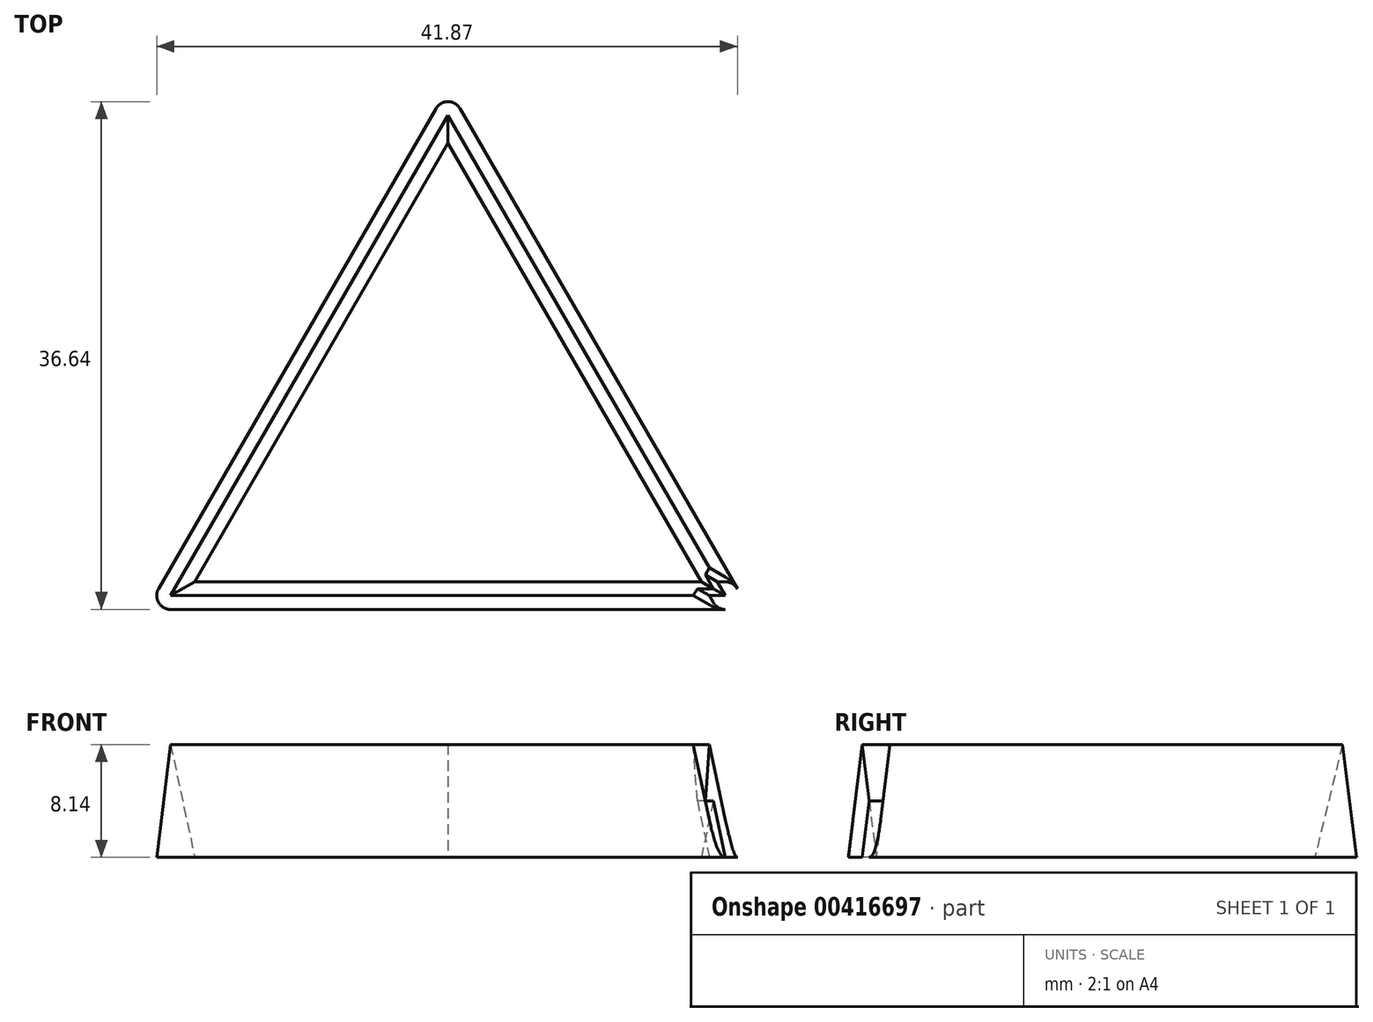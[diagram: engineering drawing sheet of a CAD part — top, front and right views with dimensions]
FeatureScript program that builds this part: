
annotation { "Feature Type Name" : "Feature", "Feature Type Description" : "" }
export const myFeature = defineFeature(function(context is Context, id is Id, definition is map)
    precondition{}
    {
        {
            var Q0;
            Q0=qCreatedBy(makeId("Top.planeOp"),FACE);
            var sketch = newSketch(context, id + "F0", { "sketchPlane" : qUnion([Q0])});
            skPoint(sketch, "E0", {"position": v(0, 0) * mm});
            skPoint(sketch, "E1", {"position": v(-20, -34.64) * mm});
            skPoint(sketch, "E2", {"position": v(20, -34.64) * mm});
            skLineSegment(sketch, "E3", {"start": v(0, 0) * mm, "end": v(-20, -34.64) * mm});
            skLineSegment(sketch, "E4", {"start": v(-20, -34.64) * mm, "end": v(20, -34.64) * mm});
            skLineSegment(sketch, "E5", {"start": v(20, -34.64) * mm, "end": v(0, 0) * mm});
            skArc(sketch, "E6.0.startCap", {"start": v(-0.87, 0.5) * mm, "mid": v(0.5, 0.87) * mm, "end": v(0.87, -0.5) * mm});
            skArc(sketch, "E6.0.endCap", {"start": v(-19.13, -35.14) * mm, "mid": v(-20.5, -35.5) * mm, "end": v(-20.87, -34.14) * mm});
            skLineSegment(sketch, "E6.0.left", {"start": v(0.87, -0.5) * mm, "end": v(-19.13, -35.14) * mm});
            skLineSegment(sketch, "E6.0.right", {"start": v(-0.87, 0.5) * mm, "end": v(-20.87, -34.14) * mm});
            skArc(sketch, "E6.1.startCap", {"start": v(-20, -35.64) * mm, "mid": v(-21, -34.64) * mm, "end": v(-20, -33.64) * mm});
            skArc(sketch, "E6.1.endCap", {"start": v(20, -33.64) * mm, "mid": v(21, -34.64) * mm, "end": v(20, -35.64) * mm});
            skLineSegment(sketch, "E6.1.left", {"start": v(-20, -33.64) * mm, "end": v(20, -33.64) * mm});
            skLineSegment(sketch, "E6.1.right", {"start": v(-20, -35.64) * mm, "end": v(20, -35.64) * mm});
            skArc(sketch, "E6.2.startCap", {"start": v(20.87, -34.14) * mm, "mid": v(20.5, -35.5) * mm, "end": v(19.13, -35.14) * mm});
            skArc(sketch, "E6.2.endCap", {"start": v(-0.87, -0.5) * mm, "mid": v(-0.5, 0.87) * mm, "end": v(0.87, 0.5) * mm});
            skLineSegment(sketch, "E6.2.left", {"start": v(19.13, -35.14) * mm, "end": v(-0.87, -0.5) * mm});
            skLineSegment(sketch, "E6.2.right", {"start": v(20.87, -34.14) * mm, "end": v(0.87, 0.5) * mm});
            skSolve(sketch);
        }
        {
            var Q0;
            {var subQ1=sQuery(id+"F0.wireOp",EDGE,"E6.0.endCap");Q0=makeQuery(id+"F0.imprint","IMPRINT",FACE,{"disambiguationData":[TD([[makeQuery(id+"F0.imprint","IMPRINT",EDGE,{"derivedFrom":subQ1}),-1.0]])]});}
            var Q1;
            {var subQ0=sQuery(id+"F0.wireOp",EDGE,"E4");var subQ1=sQuery(id+"F0.wireOp",EDGE,"E3");var subQ2=makeQuery(id+"F0.imprint","INTERSECT",VERTEX,{"derivedFrom":[subQ1,subQ0]});Q1=makeQuery(id+"F0.imprint","IMPRINT",FACE,{"disambiguationData":[TD([[makeQuery(id+"F0.imprint","IMPRINT",EDGE,{"disambiguationData":[TD([[subQ2,1.0]])],"derivedFrom":subQ1}),1.0]])]});}
            var Q2;
            {var subQ1=sQuery(id+"F0.wireOp",EDGE,"E6.0.startCap");Q2=makeQuery(id+"F0.imprint","IMPRINT",FACE,{"disambiguationData":[TD([[makeQuery(id+"F0.imprint","IMPRINT",EDGE,{"derivedFrom":subQ1}),-1.0]])]});}
            var Q3;
            {var subQ5=sQuery(id+"F0.wireOp",EDGE,"E6.0.right");Q3=makeQuery(id+"F0.imprint","IMPRINT",FACE,{"disambiguationData":[TD([[makeQuery(id+"F0.imprint","IMPRINT",EDGE,{"derivedFrom":subQ5}),1.0]])]});}
            var Q4;
            {var subQ0=sQuery(id+"F0.wireOp",EDGE,"E6.2.left");var subQ1=sQuery(id+"F0.wireOp",EDGE,"E3");var subQ2=makeQuery(id+"F0.imprint","INTERSECT",VERTEX,{"derivedFrom":[subQ1,subQ0]});Q4=makeQuery(id+"F0.imprint","IMPRINT",FACE,{"disambiguationData":[TD([[makeQuery(id+"F0.imprint","IMPRINT",EDGE,{"disambiguationData":[TD([[subQ2,-1.0]])],"derivedFrom":subQ1}),1.0]])]});}
            var Q5;
            {var subQ0=sQuery(id+"F0.wireOp",EDGE,"E5");var subQ1=sQuery(id+"F0.wireOp",EDGE,"E3");var subQ2=makeQuery(id+"F0.imprint","INTERSECT",VERTEX,{"derivedFrom":[subQ1,subQ0]});Q5=makeQuery(id+"F0.imprint","IMPRINT",FACE,{"disambiguationData":[TD([[makeQuery(id+"F0.imprint","IMPRINT",EDGE,{"disambiguationData":[TD([[subQ2,-1.0]])],"derivedFrom":subQ1}),1.0]])]});}
            var Q6;
            {var subQ1=sQuery(id+"F0.wireOp",EDGE,"E6.0.startCap");Q6=makeQuery(id+"F0.imprint","IMPRINT",FACE,{"disambiguationData":[TD([[makeQuery(id+"F0.imprint","IMPRINT",EDGE,{"derivedFrom":subQ1}),1.0]])]});}
            var Q7;
            {var subQ0=sQuery(id+"F0.wireOp",EDGE,"E6.0.left");var subQ1=sQuery(id+"F0.wireOp",EDGE,"E4");var subQ2=makeQuery(id+"F0.imprint","INTERSECT",VERTEX,{"derivedFrom":[subQ1,subQ0]});Q7=makeQuery(id+"F0.imprint","IMPRINT",FACE,{"disambiguationData":[TD([[makeQuery(id+"F0.imprint","IMPRINT",EDGE,{"disambiguationData":[TD([[subQ2,-1.0]])],"derivedFrom":subQ1}),1.0]])]});}
            var Q8;
            {var subQ0=sQuery(id+"F0.wireOp",EDGE,"E6.1.left");var subQ1=sQuery(id+"F0.wireOp",EDGE,"E5");var subQ2=makeQuery(id+"F0.imprint","INTERSECT",VERTEX,{"derivedFrom":[subQ1,subQ0]});Q8=makeQuery(id+"F0.imprint","IMPRINT",FACE,{"disambiguationData":[TD([[makeQuery(id+"F0.imprint","IMPRINT",EDGE,{"disambiguationData":[TD([[subQ2,-1.0]])],"derivedFrom":subQ1}),1.0]])]});}
            var Q9;
            {var subQ0=sQuery(id+"F0.wireOp",EDGE,"E5");var subQ1=sQuery(id+"F0.wireOp",EDGE,"E4");var subQ2=makeQuery(id+"F0.imprint","INTERSECT",VERTEX,{"derivedFrom":[subQ1,subQ0]});Q9=makeQuery(id+"F0.imprint","IMPRINT",FACE,{"disambiguationData":[TD([[makeQuery(id+"F0.imprint","IMPRINT",EDGE,{"disambiguationData":[TD([[subQ2,1.0]])],"derivedFrom":subQ1}),1.0]])]});}
            var Q10;
            {var subQ2=sQuery(id+"F0.wireOp",EDGE,"E6.0.endCap");Q10=makeQuery(id+"F0.imprint","IMPRINT",FACE,{"disambiguationData":[TD([[makeQuery(id+"F0.imprint","IMPRINT",EDGE,{"derivedFrom":subQ2}),1.0]])]});}
            var Q11;
            {var subQ1=sQuery(id+"F0.wireOp",EDGE,"E6.1.endCap");Q11=makeQuery(id+"F0.imprint","IMPRINT",FACE,{"disambiguationData":[TD([[makeQuery(id+"F0.imprint","IMPRINT",EDGE,{"derivedFrom":subQ1}),-1.0]])]});}
            extrude(context, id + "F1", {"entities" : qUnion([Q0, Q1, Q2, Q3, Q4, Q5, Q6, Q7, Q8, Q9, Q10, Q11]), "depth" : 10 * mm, "hasDraft" : true, "draftAngle" : 7 * degree, "draftPullDirection" : true});
        }
    });
